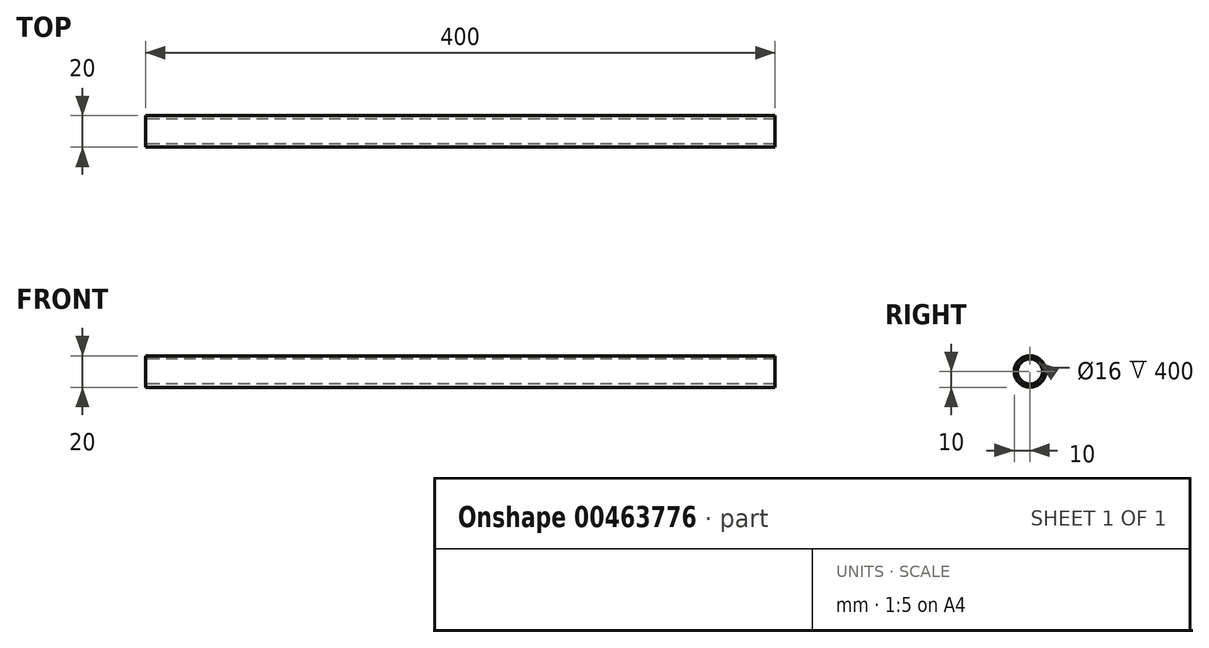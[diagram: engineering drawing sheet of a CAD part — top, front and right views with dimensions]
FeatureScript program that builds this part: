
annotation { "Feature Type Name" : "Feature", "Feature Type Description" : "" }
export const myFeature = defineFeature(function(context is Context, id is Id, definition is map)
    precondition{}
    {
        {
            var Q0;
            Q0=qCreatedBy(makeId("Right.planeOp"),FACE);
            var sketch = newSketch(context, id + "F0", { "sketchPlane" : qUnion([Q0])});
            skCircle(sketch, "E0", {"center": v(0, 0) * mm, "radius": 10 * mm});
            skCircle(sketch, "E1", {"center": v(0, 0) * mm, "radius": 8 * mm});
            skSolve(sketch);
        }
        {
            var Q0;
            Q0 = qSketchRegion(id + "F0", true);
            extrude(context, id + "F1", {"entities" : qUnion([Q0]), "depth" : 400 * mm});
        }
    });
